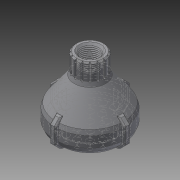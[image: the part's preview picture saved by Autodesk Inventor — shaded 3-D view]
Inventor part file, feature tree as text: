
AUTODESK INVENTOR PART (.ipt)
format: ipt  version: 2013 SP1 (Build 170176100, 176)  size: 975,872 bytes
history: native  units: in
note: dims shown in document units (in); Inventor stores cm internally (conversion verified against a paired STEP export)
features: sketch x20, extrude x18, chamfer x14, helix x1, fillet x1
ambient origin geometry x8: Origin, YZ Plane, XZ Plane, XY Plane, X Axis, Y Axis, Z Axis, Center Point
bodies: Solid1 (feature_tree)
feature tree (54):
  extrude  "Extrusion1"  Depth=0.25in TaperAngle=0.0deg
  extrude  "Extrusion2"  Depth=2.0in TaperAngle=0.0deg
  extrude  "Extrusion3"  Depth=1.625in TaperAngle=45.0deg
  chamfer  "Chamfer1"  Distance=1.625in Angle=45.0deg
  chamfer  "Chamfer2"  Distance=0.2in Angle=45.0deg
  chamfer  "Chamfer3"  Distance=0.25in
  extrude  "Extrusion4"  Depth=0.0225in TaperAngle=45.0deg
  extrude  "Extrusion5"  Depth=0.75in TaperAngle=0.0deg
  extrude  "Extrusion6"  Depth=0.05in
  chamfer  "Chamfer4"  Distance=0.05in
  chamfer  "Chamfer5"  Distance=0.05in Angle=45.0deg
  extrude  "Extrusion7"  Depth=0.05in TaperAngle=0.0deg
  chamfer  "Chamfer6"  Distance=0.125in Angle=45.0deg
  extrude  "Extrusion8"  Depth=0.25in TaperAngle=45.0deg
  chamfer  "Chamfer7"  Distance=0.05in Angle=45.0deg
  chamfer  "Chamfer8"  Distance=0.1in Angle=45.0deg
  extrude  "Extrusion9"  Depth=0.6in TaperAngle=0.0deg
  chamfer  "Chamfer9"  Distance=0.6in
  extrude  "Extrusion10"  Depth=0.05in TaperAngle=0.0deg
  chamfer  "Chamfer10"  Distance=0.05in Angle=45.0deg
  chamfer  "Chamfer11"  Distance=2.5in
  chamfer  "Chamfer12"  Distance=0.6in
  chamfer  "Chamfer13"  Distance=0.1in
  extrude  "Extrusion17"  Depth=0.125in
  extrude  "Extrusion11"  [1 undecoded]
  helix  "Coil1"  [1 undecoded]
  extrude  "Extrusion12"  [1 undecoded]
  extrude  "Extrusion13"  [1 undecoded]
  extrude  "Extrusion14"  [1 undecoded]
  chamfer  "Chamfer14"  [1 undecoded]
  extrude  "Extrusion16"  [1 undecoded]
  extrude  "Extrusion18"  [1 undecoded]
  extrude  "Extrusion19"  [1 undecoded]
  fillet  "Fillet1"  [1 undecoded]
  sketch  "Sketch1"  dims[d0=3.0in d1=0.25in d2=0.0in]
  sketch  "Sketch2"  dims[d3=2.6in d4=2.0in d5=0.0in]
  sketch  "Sketch3"  dims[d6=0.25in d7=0.0in d8=1.625in d9=1.1875in d10=45.0deg d11=1.625in d12=1.1875in d13=45.0deg d14=0.2in d15=1.1875in d16=45.0deg]
  sketch  "Sketch4"  dims[d17=1.25in]
  sketch  "Sketch5"  dims[d18=0.375in d19=0.5in d20=0.0in d21=0.0in d22=0.25in d23=0.0in]
  sketch  "Sketch6"  dims[d24=0.25in d25=0.0in d26=0.0225in d27=1.1875in d28=45.0deg]
  sketch  "Sketch7"  dims[d31=0.06in d32=1.1875in d33=45.0deg d34=0.75in d35=0.0in]
  sketch  "Sketch8"  dims[d36=0.036in d37=1.1875in d38=45.0deg d39=0.05in d40=0.05in d41=0.0in d42=0.05in d43=1.1875in d44=45.0deg]
  sketch  "Sketch9"  dims[d45=0.05in d46=1.1875in d47=45.0deg d48=0.05in d49=0.5in d50=0.0in d51=0.125in d52=1.1875in d53=45.0deg]
  sketch  "Sketch10"  dims[d54=1.2in d55=0.0in d56=0.25in d57=1.1875in d58=45.0deg d59=0.05in d60=1.1875in d61=45.0deg d62=0.1in d63=1.1875in d64=45.0deg]
  sketch  "Sketch11"  dims[d65=0.01in d66=1.1875in d67=45.0deg d68=0.6in d69=0.0in]
  sketch  "Sketch12"  dims[d70=0.6in]
  sketch  "Sketch14"  dims[d71=0.0689in d72=0.7in d73=3.8583in d74=-0.0034in d75=90.0deg d76=90.0deg d77=90.0deg d78=90.0deg d79=0.6in d80=0.0in]
  sketch  "Sketch15"  dims[d81=0.05in d82=0.0in d83=0.05in d84=0.0in d85=0.05in d86=1.1875in d87=45.0deg d90=2.5in d91=0.0in]
  sketch  "Sketch16"  dims[d92=0.74in d93=0.6in d94=0.0in d96=0.1in d97=-0.3092in]
  sketch  "Sketch17"  dims[d101=0.03in d102=0.0in d105=0.125in]
  sketch  "Sketch19"
  sketch  "Sketch20"
  sketch  "Sketch21"
  sketch  "Sketch22"
note: 10 required parameter values undecoded (feature->parameter linkage not recoverable at this tier; creation-order binding heuristic only, values carry confidence <= 0.55)
